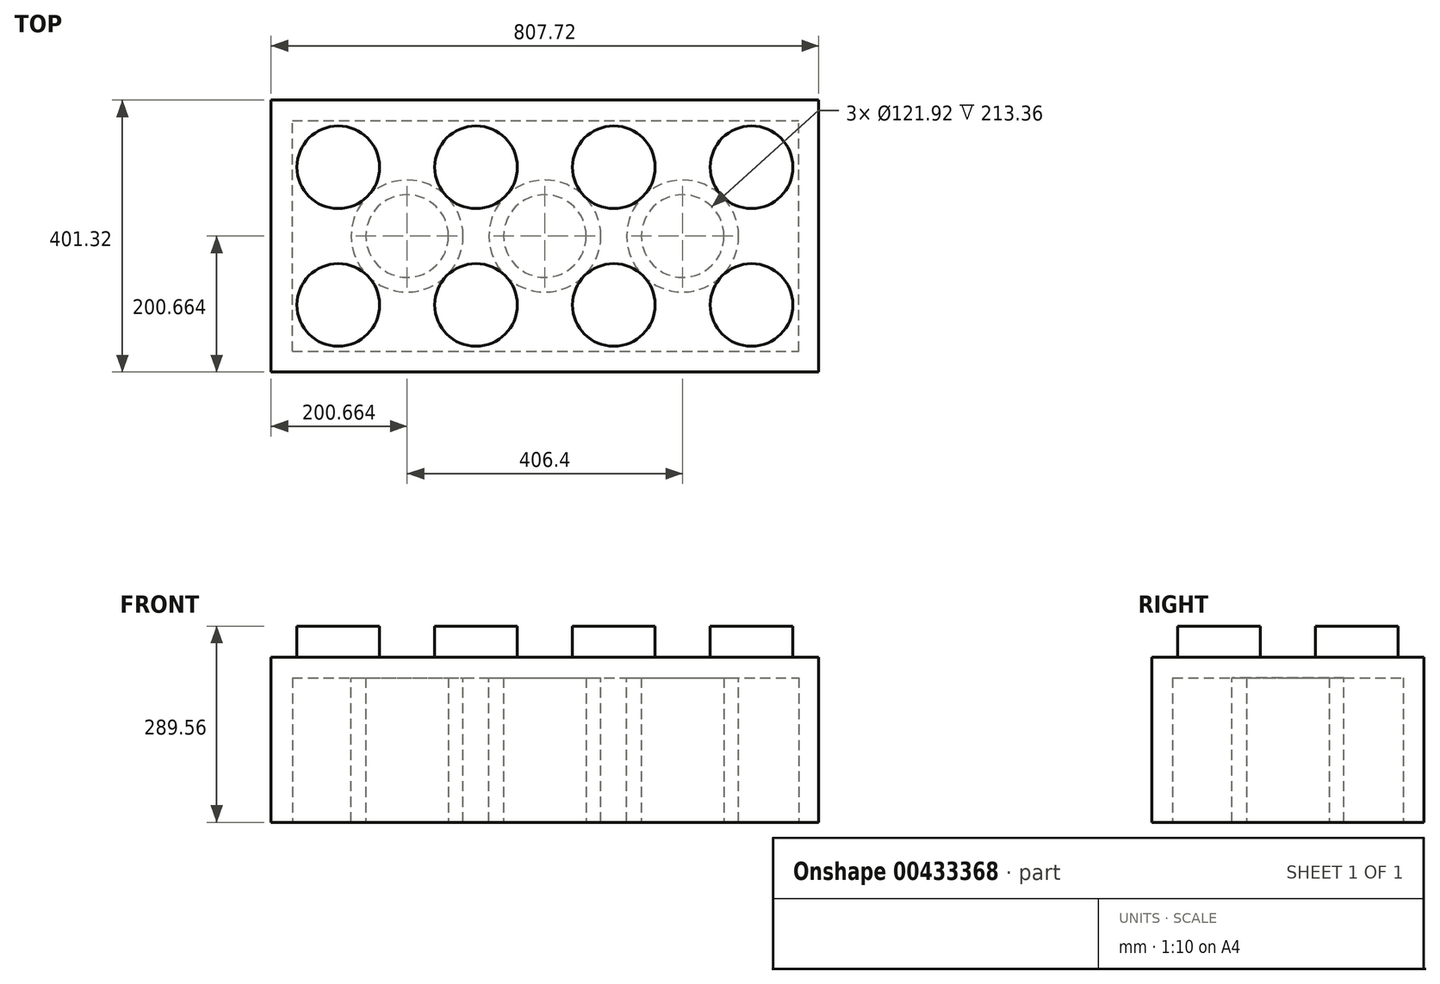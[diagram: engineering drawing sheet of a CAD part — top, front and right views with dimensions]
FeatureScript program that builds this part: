
annotation { "Feature Type Name" : "Feature", "Feature Type Description" : "" }
export const myFeature = defineFeature(function(context is Context, id is Id, definition is map)
    precondition{}
    {
        {
            var Q0;
            Q0=qCreatedBy(makeId("Top.planeOp"),FACE);
            var sketch = newSketch(context, id + "F0", { "sketchPlane" : qUnion([Q0])});
            skLineSegment(sketch, "E0.bottom", {"start": v(-406.83, 196.66) * mm, "end": v(400.9, 196.66) * mm});
            skLineSegment(sketch, "E0.top", {"start": v(-406.83, -204.66) * mm, "end": v(400.9, -204.66) * mm});
            skLineSegment(sketch, "E0.left", {"start": v(-406.83, 196.66) * mm, "end": v(-406.83, -204.66) * mm});
            skLineSegment(sketch, "E0.right", {"start": v(400.9, 196.66) * mm, "end": v(400.9, -204.66) * mm});
            skSolve(sketch);
        }
        {
            var Q0;
            Q0 = qSketchRegion(id + "F0", true);
            extrude(context, id + "F1", {"entities" : qUnion([Q0]), "depth" : 243.84 * mm});
        }
        {
            var Q0;
            Q0=makeQuery(id+"F1.opExtrude","CAP_FACE",FACE,{"disambiguationData":[OSD([sQuery(id+"F0.wireOp",EDGE,"E0.bottom"),sQuery(id+"F0.wireOp",EDGE,"E0.top"),sQuery(id+"F0.wireOp",EDGE,"E0.left"),sQuery(id+"F0.wireOp",EDGE,"E0.right")])],"isStart":false});
            var sketch = newSketch(context, id + "F2", { "sketchPlane" : qUnion([Q0])});
            skCircle(sketch, "E1", {"center": v(-307.77, 97.6) * mm, "radius": 60.96 * mm});
            skCircle(sketch, "E2.0.1.0", {"center": v(-307.77, -105.6) * mm, "radius": 60.96 * mm});
            skCircle(sketch, "E2.1.0.0", {"center": v(-104.57, 97.6) * mm, "radius": 60.96 * mm});
            skCircle(sketch, "E2.1.1.0", {"center": v(-104.57, -105.6) * mm, "radius": 60.96 * mm});
            skCircle(sketch, "E2.2.0.0", {"center": v(98.63, 97.6) * mm, "radius": 60.96 * mm});
            skCircle(sketch, "E2.2.1.0", {"center": v(98.63, -105.6) * mm, "radius": 60.96 * mm});
            skCircle(sketch, "E2.3.0.0", {"center": v(301.83, 97.6) * mm, "radius": 60.96 * mm});
            skCircle(sketch, "E2.3.1.0", {"center": v(301.83, -105.6) * mm, "radius": 60.96 * mm});
            skLineSegment(sketch, "E2.direction1", {"start": v(-307.77, 97.6) * mm, "end": v(-104.57, 97.6) * mm, "construction": true});
            skLineSegment(sketch, "E2.direction2", {"start": v(-307.77, 97.6) * mm, "end": v(-307.77, -105.6) * mm, "construction": true});
            skSolve(sketch);
        }
        {
            var Q0;
            Q0=makeQuery(id+"F2.imprint","IMPRINT",FACE,{"disambiguationData":[TD([[makeQuery(id+"F2.imprint","IMPRINT",EDGE,{"derivedFrom":sQuery(id+"F2.wireOp",EDGE,"E1")}),1.0]])]});
            var Q1;
            Q1=makeQuery(id+"F2.imprint","IMPRINT",FACE,{"disambiguationData":[TD([[makeQuery(id+"F2.imprint","IMPRINT",EDGE,{"derivedFrom":sQuery(id+"F2.wireOp",EDGE,"E2.0.1.0")}),1.0]])]});
            var Q2;
            Q2=makeQuery(id+"F2.imprint","IMPRINT",FACE,{"disambiguationData":[TD([[makeQuery(id+"F2.imprint","IMPRINT",EDGE,{"derivedFrom":sQuery(id+"F2.wireOp",EDGE,"E2.1.1.0")}),1.0]])]});
            var Q3;
            Q3=makeQuery(id+"F2.imprint","IMPRINT",FACE,{"disambiguationData":[TD([[makeQuery(id+"F2.imprint","IMPRINT",EDGE,{"derivedFrom":sQuery(id+"F2.wireOp",EDGE,"E2.1.0.0")}),1.0]])]});
            var Q4;
            Q4=makeQuery(id+"F2.imprint","IMPRINT",FACE,{"disambiguationData":[TD([[makeQuery(id+"F2.imprint","IMPRINT",EDGE,{"derivedFrom":sQuery(id+"F2.wireOp",EDGE,"E2.2.0.0")}),1.0]])]});
            var Q5;
            Q5=makeQuery(id+"F2.imprint","IMPRINT",FACE,{"disambiguationData":[TD([[makeQuery(id+"F2.imprint","IMPRINT",EDGE,{"derivedFrom":sQuery(id+"F2.wireOp",EDGE,"E2.2.1.0")}),1.0]])]});
            var Q6;
            Q6=makeQuery(id+"F2.imprint","IMPRINT",FACE,{"disambiguationData":[TD([[makeQuery(id+"F2.imprint","IMPRINT",EDGE,{"derivedFrom":sQuery(id+"F2.wireOp",EDGE,"E2.3.1.0")}),1.0]])]});
            var Q7;
            Q7=makeQuery(id+"F2.imprint","IMPRINT",FACE,{"disambiguationData":[TD([[makeQuery(id+"F2.imprint","IMPRINT",EDGE,{"derivedFrom":sQuery(id+"F2.wireOp",EDGE,"E2.3.0.0")}),1.0]])]});
            extrude(context, id + "F3", {"entities" : qUnion([Q0, Q1, Q2, Q3, Q4, Q5, Q6, Q7]), "operationType" : NewBodyOperationType.ADD, "depth" : 45.72 * mm});
        }
        {
            var Q0;
            Q0=makeQuery(id+"F1.opExtrude","CAP_FACE",FACE,{"disambiguationData":[OSD([sQuery(id+"F0.wireOp",EDGE,"E0.bottom"),sQuery(id+"F0.wireOp",EDGE,"E0.top"),sQuery(id+"F0.wireOp",EDGE,"E0.left"),sQuery(id+"F0.wireOp",EDGE,"E0.right")])],"isStart":true});
            var sketch = newSketch(context, id + "F4", { "sketchPlane" : qUnion([Q0])});
            skLineSegment(sketch, "E3.bottom", {"start": v(-375.37, 174.18) * mm, "end": v(371.39, 174.18) * mm});
            skLineSegment(sketch, "E3.top", {"start": v(-375.37, -166.18) * mm, "end": v(371.39, -166.18) * mm});
            skLineSegment(sketch, "E3.left", {"start": v(-375.37, 174.18) * mm, "end": v(-375.37, -166.18) * mm});
            skLineSegment(sketch, "E3.right", {"start": v(371.39, 174.18) * mm, "end": v(371.39, -166.18) * mm});
            skSolve(sketch);
        }
        {
            var Q0;
            Q0=makeQuery(id+"F4.imprint","IMPRINT",FACE,{"disambiguationData":[TD([[makeQuery(id+"F4.imprint","IMPRINT",EDGE,{"derivedFrom":sQuery(id+"F4.wireOp",EDGE,"E3.bottom")}),-1.0]])]});
            extrude(context, id + "F5", {"entities" : qUnion([Q0]), "operationType" : NewBodyOperationType.REMOVE, "oppositeDirection" : true, "depth" : 213.36 * mm});
        }
        {
            var Q0;
            Q0=makeQuery(id+"F5.boolean.opBoolean","COPY",FACE,{"derivedFrom":makeQuery(id+"F5.opExtrude","CAP_FACE",FACE,{"disambiguationData":[OSD([sQuery(id+"F4.wireOp",EDGE,"E3.bottom"),sQuery(id+"F4.wireOp",EDGE,"E3.top"),sQuery(id+"F4.wireOp",EDGE,"E3.left"),sQuery(id+"F4.wireOp",EDGE,"E3.right")])],"isStart":false})});
            var sketch = newSketch(context, id + "F6", { "sketchPlane" : qUnion([Q0])});
            skCircle(sketch, "E4", {"center": v(-206.17, 4) * mm, "radius": 82.55 * mm});
            skCircle(sketch, "E5.1.0.0", {"center": v(-2.97, 4) * mm, "radius": 82.55 * mm});
            skCircle(sketch, "E5.2.0.0", {"center": v(200.23, 4) * mm, "radius": 82.55 * mm});
            skLineSegment(sketch, "E5.direction1", {"start": v(-206.17, 4) * mm, "end": v(-2.97, 4) * mm, "construction": true});
            skSolve(sketch);
        }
        {
            var Q0;
            Q0 = qSketchRegion(id + "F6", true);
            extrude(context, id + "F7", {"entities" : qUnion([Q0]), "operationType" : NewBodyOperationType.ADD, "depth" : 213.36 * mm});
        }
        {
            var Q0;
            Q0=makeQuery(id+"F7.opExtrude","CAP_FACE",FACE,{"disambiguationData":[OSD([sQuery(id+"F6.wireOp",EDGE,"E4")])],"isStart":false});
            var sketch = newSketch(context, id + "F8", { "sketchPlane" : qUnion([Q0])});
            skCircle(sketch, "E6", {"center": v(-206.17, 4) * mm, "radius": 60.96 * mm});
            skCircle(sketch, "E7.1.0.0", {"center": v(-2.97, 4) * mm, "radius": 60.96 * mm});
            skCircle(sketch, "E7.2.0.0", {"center": v(200.23, 4) * mm, "radius": 60.96 * mm});
            skLineSegment(sketch, "E7.direction1", {"start": v(-206.17, 4) * mm, "end": v(-2.97, 4) * mm, "construction": true});
            skSolve(sketch);
        }
        {
            var Q0;
            Q0 = qSketchRegion(id + "F8", true);
            extrude(context, id + "F9", {"entities" : qUnion([Q0]), "operationType" : NewBodyOperationType.REMOVE, "oppositeDirection" : true, "depth" : 213.36 * mm});
        }
    });
